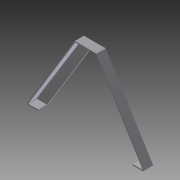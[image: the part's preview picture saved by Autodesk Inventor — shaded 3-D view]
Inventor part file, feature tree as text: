
AUTODESK INVENTOR PART (.ipt)
format: ipt  version: 2012 (Build 160160000, 160)  size: 139,264 bytes
history: native  units: in
note: dims shown in document units (in); Inventor stores cm internally (conversion verified against a paired STEP export)
features: extrude x2, fillet x2, sketch x1
ambient origin geometry x8: Origin, YZ Plane, XZ Plane, XY Plane, X Axis, Y Axis, Z Axis, Center Point
bodies: Solid1 (feature_tree)
feature tree (5):
  sketch  "Sketch1"  dims[d0=13.0in d1=2.25in d4=0.125in d5=0.125in d6=8.5in d10=1.0in d11=0.0in d12=0.125in d13=0.0in d14=0.0312in d15=0.125in d29=0.4013in d30=0.4013in d31=0.125in d34=1.0in d35=1.0in d36=0.0625in d37=0.0625in d38=0.0625in d39=0.0625in d40=0.4013in d41=0.125in d42=0.0625in]
  extrude  "Extrusion1"  Depth=2.25in
  extrude  "Extrusion2"  Depth=0.125in
  fillet  "Fillet1"  Radius=0.125in
  fillet  "Fillet2"  Radius=8.5in
